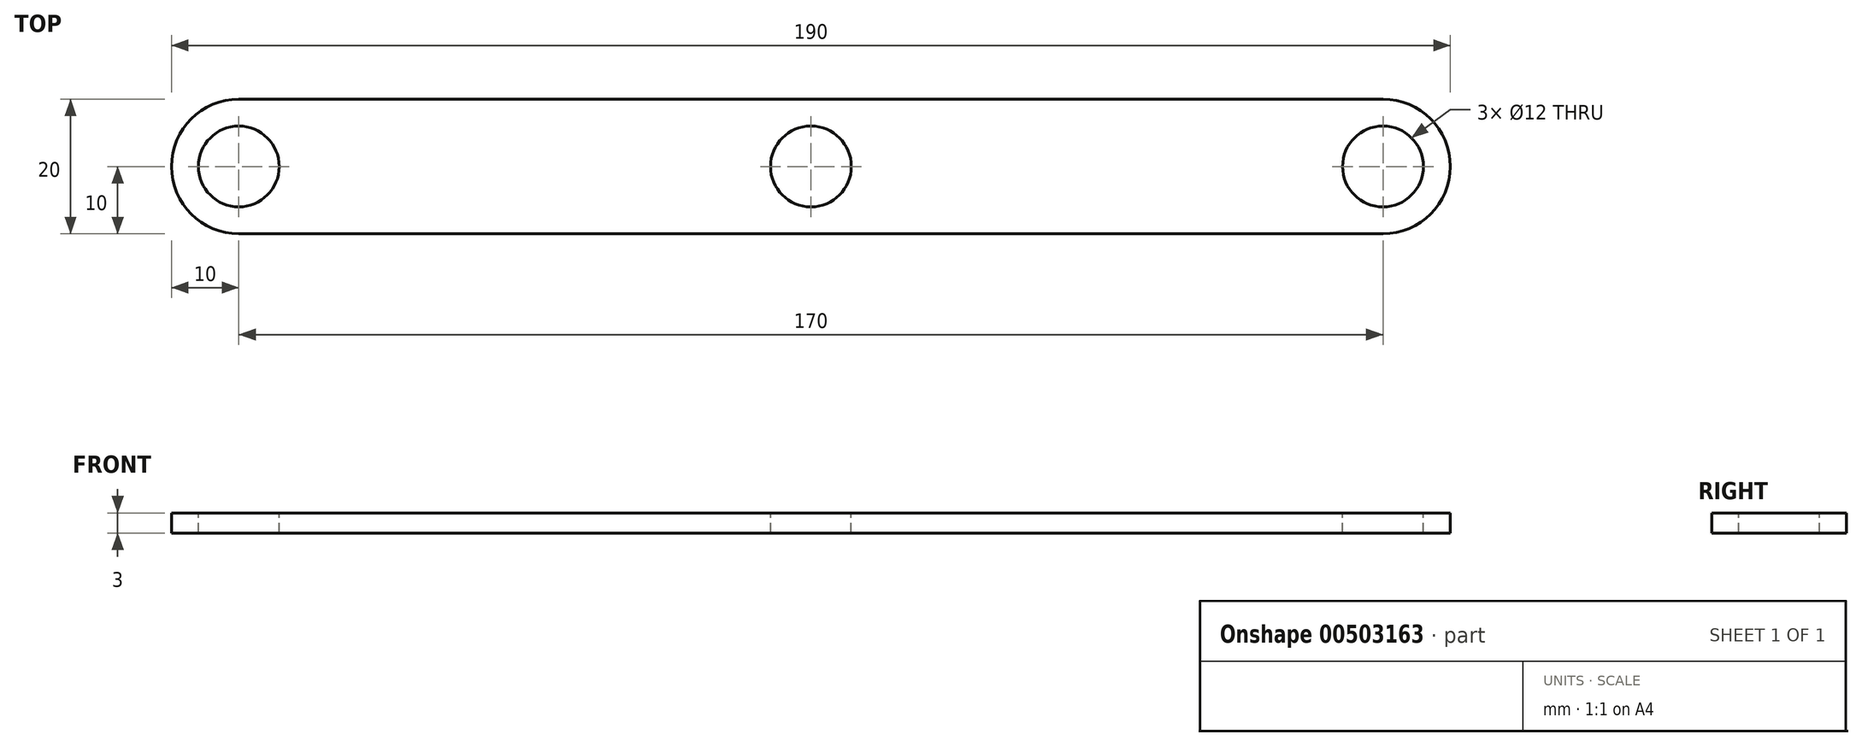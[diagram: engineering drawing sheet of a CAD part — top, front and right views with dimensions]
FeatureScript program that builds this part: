
annotation { "Feature Type Name" : "Feature", "Feature Type Description" : "" }
export const myFeature = defineFeature(function(context is Context, id is Id, definition is map)
    precondition{}
    {
        {
            var Q0;
            Q0=qCreatedBy(makeId("Top.planeOp"),FACE);
            var sketch = newSketch(context, id + "F0", { "sketchPlane" : qUnion([Q0])});
            skLineSegment(sketch, "E0.bottom", {"start": v(95, 10) * mm, "end": v(-95, 10) * mm});
            skLineSegment(sketch, "E0.top", {"start": v(95, -10) * mm, "end": v(-95, -10) * mm});
            skLineSegment(sketch, "E0.left", {"start": v(95, 10) * mm, "end": v(95, -10) * mm});
            skLineSegment(sketch, "E0.right", {"start": v(-95, 10) * mm, "end": v(-95, -10) * mm});
            skPoint(sketch, "E0.middle", {"position": v(0, 0) * mm});
            skSolve(sketch);
        }
        {
            var Q0;
            Q0=makeQuery(id+"F0.imprint","IMPRINT",FACE,{"disambiguationData":[TD([[makeQuery(id+"F0.imprint","IMPRINT",EDGE,{"derivedFrom":sQuery(id+"F0.wireOp",EDGE,"E0.bottom")}),1.0]])]});
            extrude(context, id + "F1", {"entities" : qUnion([Q0]), "endBound" : BoundingType.SYMMETRIC, "depth" : 3 * mm});
        }
        {
            var Q0;
            Q0=makeQuery(id+"F1.opExtrude","CAP_FACE",FACE,{"disambiguationData":[OSD([sQuery(id+"F0.wireOp",EDGE,"E0.bottom"),sQuery(id+"F0.wireOp",EDGE,"E0.top"),sQuery(id+"F0.wireOp",EDGE,"E0.left"),sQuery(id+"F0.wireOp",EDGE,"E0.right")])],"isStart":false});
            var sketch = newSketch(context, id + "F2", { "sketchPlane" : qUnion([Q0])});
            skLineSegment(sketch, "E1", {"start": v(-95, 0) * mm, "end": v(95, 0) * mm, "construction": true});
            skLineSegment(sketch, "E2", {"start": v(-95, 0) * mm, "end": v(-85, 0) * mm, "construction": true});
            skCircle(sketch, "E3", {"center": v(-85, 0) * mm, "radius": 6 * mm});
            skLineSegment(sketch, "E4", {"start": v(95, 0) * mm, "end": v(85, 0) * mm, "construction": true});
            skCircle(sketch, "E5", {"center": v(85, 0) * mm, "radius": 6 * mm});
            skSolve(sketch);
        }
        {
            var Q0;
            Q0=makeQuery(id+"F2.imprint","IMPRINT",FACE,{"disambiguationData":[TD([[makeQuery(id+"F2.imprint","IMPRINT",EDGE,{"derivedFrom":sQuery(id+"F2.wireOp",EDGE,"E3")}),1.0]])]});
            var Q1;
            Q1=makeQuery(id+"F2.imprint","IMPRINT",FACE,{"disambiguationData":[TD([[makeQuery(id+"F2.imprint","IMPRINT",EDGE,{"derivedFrom":sQuery(id+"F2.wireOp",EDGE,"E5")}),1.0]])]});
            extrude(context, id + "F3", {"entities" : qUnion([Q0, Q1]), "operationType" : NewBodyOperationType.REMOVE, "endBound" : BoundingType.THROUGH_ALL, "oppositeDirection" : true, "depth" : 25 * mm});
        }
        {
            var Q0;
            Q0=makeQuery(id+"F1.opExtrude","CAP_FACE",FACE,{"disambiguationData":[OSD([sQuery(id+"F0.wireOp",EDGE,"E0.bottom"),sQuery(id+"F0.wireOp",EDGE,"E0.top"),sQuery(id+"F0.wireOp",EDGE,"E0.left"),sQuery(id+"F0.wireOp",EDGE,"E0.right")])],"isStart":false});
            var sketch = newSketch(context, id + "F4", { "sketchPlane" : qUnion([Q0])});
            skLineSegment(sketch, "E6", {"start": v(-95, 0) * mm, "end": v(95, 0) * mm, "construction": true});
            skCircle(sketch, "E7", {"center": v(0, 0) * mm, "radius": 6 * mm});
            skSolve(sketch);
        }
        {
            var Q0;
            Q0=makeQuery(id+"F4.imprint","IMPRINT",FACE,{"disambiguationData":[TD([[makeQuery(id+"F4.imprint","IMPRINT",EDGE,{"derivedFrom":sQuery(id+"F4.wireOp",EDGE,"E7")}),1.0]])]});
            var Q1;
            Q1=sQuery(id+"F4.wireOp",EDGE,"E7");
            extrude(context, id + "F5", {"entities" : qUnion([Q0]), "operationType" : NewBodyOperationType.REMOVE, "surfaceEntities" : qUnion([Q1]), "endBound" : BoundingType.THROUGH_ALL, "oppositeDirection" : true, "depth" : 25 * mm});
        }
        {
            var Q0;
            Q0=makeQuery(id+"F1.opExtrude","SWEPT_EDGE",EDGE,{"disambiguationData":[OSD([sQuery(id+"F0.wireOp",EDGE,"E0.top"),sQuery(id+"F0.wireOp",EDGE,"E0.right")])]});
            var Q1;
            Q1=makeQuery(id+"F1.opExtrude","SWEPT_EDGE",EDGE,{"disambiguationData":[OSD([sQuery(id+"F0.wireOp",EDGE,"E0.bottom"),sQuery(id+"F0.wireOp",EDGE,"E0.right")])]});
            var Q2;
            Q2=makeQuery(id+"F1.opExtrude","SWEPT_EDGE",EDGE,{"disambiguationData":[OSD([sQuery(id+"F0.wireOp",EDGE,"E0.top"),sQuery(id+"F0.wireOp",EDGE,"E0.left")])]});
            var Q3;
            Q3=makeQuery(id+"F1.opExtrude","SWEPT_EDGE",EDGE,{"disambiguationData":[OSD([sQuery(id+"F0.wireOp",EDGE,"E0.bottom"),sQuery(id+"F0.wireOp",EDGE,"E0.left")])]});
            fillet(context, id + "F6", {"entities" : qUnion([Q0, Q1, Q2, Q3]), "radius" : 10 * mm, "tangentPropagation" : true, "allowEdgeOverflow" : false});
        }
    });
